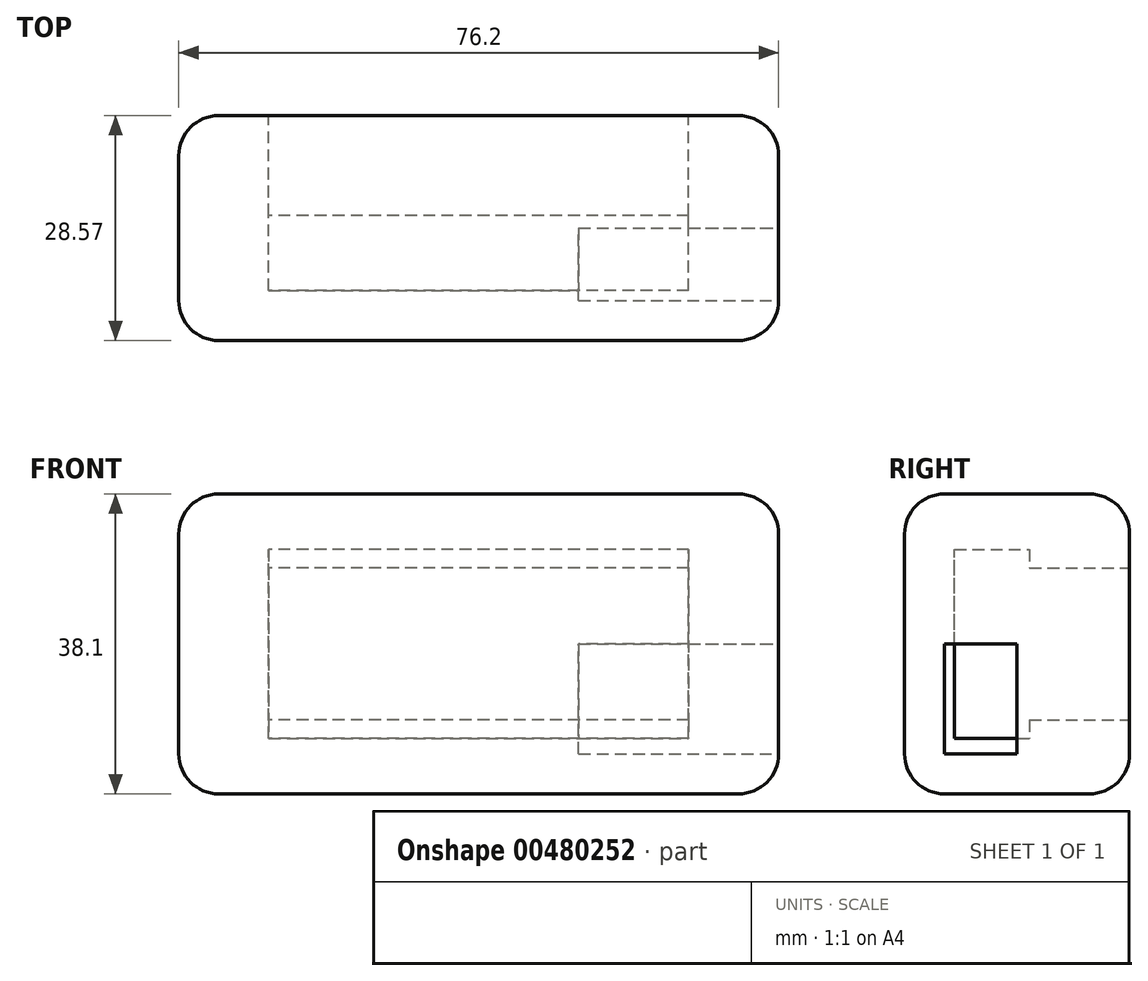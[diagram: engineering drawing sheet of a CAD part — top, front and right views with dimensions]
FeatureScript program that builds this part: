
annotation { "Feature Type Name" : "Feature", "Feature Type Description" : "" }
export const myFeature = defineFeature(function(context is Context, id is Id, definition is map)
    precondition{}
    {
        {
            var Q0;
            Q0=qCreatedBy(makeId("Front.planeOp"),FACE);
            var sketch = newSketch(context, id + "F0", { "sketchPlane" : qUnion([Q0])});
            skLineSegment(sketch, "E0.bottom", {"start": v(26.67, 9.65) * mm, "end": v(-26.67, 9.65) * mm});
            skLineSegment(sketch, "E0.top", {"start": v(26.67, -9.65) * mm, "end": v(-26.67, -9.65) * mm});
            skLineSegment(sketch, "E0.left", {"start": v(26.67, 9.65) * mm, "end": v(26.67, -9.65) * mm});
            skLineSegment(sketch, "E0.right", {"start": v(-26.67, 9.65) * mm, "end": v(-26.67, -9.65) * mm});
            skPoint(sketch, "E0.middle", {"position": v(0, 0) * mm});
            skLineSegment(sketch, "E1.bottom", {"start": v(38.1, 19.05) * mm, "end": v(-38.1, 19.05) * mm});
            skLineSegment(sketch, "E1.top", {"start": v(38.1, -19.05) * mm, "end": v(-38.1, -19.05) * mm});
            skLineSegment(sketch, "E1.left", {"start": v(38.1, 19.05) * mm, "end": v(38.1, -19.05) * mm});
            skLineSegment(sketch, "E1.right", {"start": v(-38.1, 19.05) * mm, "end": v(-38.1, -19.05) * mm});
            skSolve(sketch);
        }
        {
            var Q0;
            Q0=makeQuery(id+"F0.imprint","IMPRINT",FACE,{"disambiguationData":[TD([[makeQuery(id+"F0.imprint","IMPRINT",EDGE,{"derivedFrom":sQuery(id+"F0.wireOp",EDGE,"E0.bottom")}),-1.0]])]});
            extrude(context, id + "F1", {"entities" : qUnion([Q0]), "depth" : 12.7 * mm});
        }
        {
            var Q0;
            Q0=makeQuery(id+"F1.opExtrude","CAP_FACE",FACE,{"disambiguationData":[OSD([sQuery(id+"F0.wireOp",EDGE,"E0.bottom"),sQuery(id+"F0.wireOp",EDGE,"E0.top"),sQuery(id+"F0.wireOp",EDGE,"E0.left"),sQuery(id+"F0.wireOp",EDGE,"E0.right"),sQuery(id+"F0.wireOp",EDGE,"E1.bottom"),sQuery(id+"F0.wireOp",EDGE,"E1.top"),sQuery(id+"F0.wireOp",EDGE,"E1.left"),sQuery(id+"F0.wireOp",EDGE,"E1.right")])],"isStart":false});
            var sketch = newSketch(context, id + "F2", { "sketchPlane" : qUnion([Q0])});
            skLineSegment(sketch, "E2.bottom", {"start": v(26.67, 12) * mm, "end": v(-26.67, 12) * mm});
            skLineSegment(sketch, "E2.top", {"start": v(26.67, -12) * mm, "end": v(-26.67, -12) * mm});
            skLineSegment(sketch, "E2.left", {"start": v(26.67, 12) * mm, "end": v(26.67, -12) * mm});
            skLineSegment(sketch, "E2.right", {"start": v(-26.67, 12) * mm, "end": v(-26.67, -12) * mm});
            skPoint(sketch, "E2.middle", {"position": v(0, 0) * mm});
            skSolve(sketch);
        }
        {
            var Q0;
            {var subQ6=sQuery(id+"F2.wireOp",EDGE,"E2.bottom");Q0=makeQuery(id+"F2.imprint","IMPRINT",FACE,{"disambiguationData":[TD([[makeQuery(id+"F2.imprint","IMPRINT",EDGE,{"derivedFrom":subQ6}),-1.0]])]});}
            extrude(context, id + "F3", {"entities" : qUnion([Q0]), "operationType" : NewBodyOperationType.ADD, "depth" : 12.7 * mm});
        }
        {
            var Q0;
            Q0=makeQuery(id+"F3.opExtrude","SWEPT_FACE",FACE,{"disambiguationData":[OSD([sQuery(id+"F2.wireOp",EDGE,"E2.bottom")])]});
            var sketch = newSketch(context, id + "F4", { "sketchPlane" : qUnion([Q0])});
            skLineSegment(sketch, "E3.bottom", {"start": v(38.1, 28.58) * mm, "end": v(-38.1, 28.58) * mm});
            skLineSegment(sketch, "E3.top", {"start": v(38.1, 22.23) * mm, "end": v(-38.1, 22.23) * mm});
            skLineSegment(sketch, "E3.left", {"start": v(38.1, 28.57) * mm, "end": v(38.1, 22.23) * mm});
            skLineSegment(sketch, "E3.right", {"start": v(-38.1, 28.57) * mm, "end": v(-38.1, 22.23) * mm});
            skPoint(sketch, "E3.middle", {"position": v(0, 25.4) * mm});
            skSolve(sketch);
        }
        {
            var Q0;
            Q0=makeQuery(id+"F4.imprint","IMPRINT",FACE,{"disambiguationData":[TD([[makeQuery(id+"F4.imprint","IMPRINT",EDGE,{"derivedFrom":sQuery(id+"F4.wireOp",EDGE,"E3.bottom")}),1.0]])]});
            var Q1;
            {var subQ1=sQuery(id+"F2.wireOp",EDGE,"E2.bottom");var subQ6=makeQuery(id+"F3.opExtrude","CAP_EDGE",EDGE,{"disambiguationData":[OSD([subQ1])],"isStart":false});Q1=makeQuery(id+"F4.imprint","IMPRINT",FACE,{"disambiguationData":[TD([[makeQuery(id+"F4.imprint","IMPRINT",EDGE,{"derivedFrom":subQ6}),1.0]])]});}
            var Q2;
            {var subQ0=sQuery(id+"F0.wireOp",EDGE,"E1.top");Q2=makeQuery(id+"F3.boolean.opBoolean","MERGE",FACE,{"derivedFrom":[makeQuery(id+"F1.opExtrude","SWEPT_FACE",FACE,{"disambiguationData":[OSD([subQ0])]}),makeQuery(id+"F3.opExtrude","SWEPT_FACE",FACE,{"disambiguationData":[OSD([subQ0])]})]});}
            extrude(context, id + "F5", {"entities" : qUnion([Q0, Q1]), "operationType" : NewBodyOperationType.ADD, "endBound" : BoundingType.UP_TO_SURFACE, "endBoundEntityFace" : qUnion([Q2]), "depth" : 25.4 * mm});
        }
        {
            var Q0;
            Q0=makeQuery(id+"F5.opExtrude","CAP_FACE",FACE,{"disambiguationData":[OSD([sQuery(id+"F4.wireOp",EDGE,"E3.bottom"),sQuery(id+"F4.wireOp",EDGE,"E3.top"),sQuery(id+"F4.wireOp",EDGE,"E3.left"),sQuery(id+"F4.wireOp",EDGE,"E3.right")])],"isStart":true});
            var Q1;
            {var subQ0=sQuery(id+"F0.wireOp",EDGE,"E1.bottom");Q1=makeQuery(id+"F3.boolean.opBoolean","MERGE",FACE,{"derivedFrom":[makeQuery(id+"F1.opExtrude","SWEPT_FACE",FACE,{"disambiguationData":[OSD([subQ0])]}),makeQuery(id+"F3.opExtrude","SWEPT_FACE",FACE,{"disambiguationData":[OSD([subQ0])]})]});}
            extrude(context, id + "F6", {"entities" : qUnion([Q0]), "operationType" : NewBodyOperationType.ADD, "endBound" : BoundingType.UP_TO_SURFACE, "endBoundEntityFace" : qUnion([Q1]), "depth" : 25.4 * mm});
        }
        {
            var Q0;
            Q0=makeQuery(id+"F1.opExtrude","CAP_EDGE",EDGE,{"disambiguationData":[OSD([sQuery(id+"F0.wireOp",EDGE,"E1.bottom")])],"isStart":true});
            var Q1;
            {var subQ0=sQuery(id+"F0.wireOp",EDGE,"E1.left");var subQ1=sQuery(id+"F0.wireOp",EDGE,"E1.bottom");Q1=makeQuery(id+"F6.boolean.opBoolean","MERGE",EDGE,{"derivedFrom":[makeQuery(id+"F3.boolean.opBoolean","MERGE",EDGE,{"derivedFrom":[makeQuery(id+"F1.opExtrude","SWEPT_EDGE",EDGE,{"disambiguationData":[OSD([subQ1,subQ0])]}),makeQuery(id+"F3.opExtrude","SWEPT_EDGE",EDGE,{"disambiguationData":[OSD([subQ1,subQ0])]})]}),makeQuery(id+"F6.opExtrude","CAP_EDGE",EDGE,{"disambiguationData":[OSD([sQuery(id+"F4.wireOp",EDGE,"E3.left")])],"isStart":false})]});}
            var Q2;
            Q2=makeQuery(id+"F6.opExtrude","CAP_EDGE",EDGE,{"disambiguationData":[OSD([sQuery(id+"F4.wireOp",EDGE,"E3.bottom")])],"isStart":false});
            var Q3;
            {var subQ0=sQuery(id+"F0.wireOp",EDGE,"E1.right");var subQ1=sQuery(id+"F0.wireOp",EDGE,"E1.bottom");Q3=makeQuery(id+"F6.boolean.opBoolean","MERGE",EDGE,{"derivedFrom":[makeQuery(id+"F3.boolean.opBoolean","MERGE",EDGE,{"derivedFrom":[makeQuery(id+"F1.opExtrude","SWEPT_EDGE",EDGE,{"disambiguationData":[OSD([subQ1,subQ0])]}),makeQuery(id+"F3.opExtrude","SWEPT_EDGE",EDGE,{"disambiguationData":[OSD([subQ1,subQ0])]})]}),makeQuery(id+"F6.opExtrude","CAP_EDGE",EDGE,{"disambiguationData":[OSD([sQuery(id+"F4.wireOp",EDGE,"E3.right")])],"isStart":false})]});}
            var Q4;
            Q4=makeQuery(id+"F1.opExtrude","CAP_EDGE",EDGE,{"disambiguationData":[OSD([sQuery(id+"F0.wireOp",EDGE,"E1.right")])],"isStart":true});
            var Q5;
            Q5=makeQuery(id+"F1.opExtrude","CAP_EDGE",EDGE,{"disambiguationData":[OSD([sQuery(id+"F0.wireOp",EDGE,"E1.left")])],"isStart":true});
            var Q6;
            Q6=makeQuery(id+"F1.opExtrude","CAP_EDGE",EDGE,{"disambiguationData":[OSD([sQuery(id+"F0.wireOp",EDGE,"E1.top")])],"isStart":true});
            var Q7;
            {var subQ0=sQuery(id+"F0.wireOp",EDGE,"E1.left");var subQ1=sQuery(id+"F0.wireOp",EDGE,"E1.top");Q7=makeQuery(id+"F5.boolean.opBoolean","MERGE",EDGE,{"derivedFrom":[makeQuery(id+"F3.boolean.opBoolean","MERGE",EDGE,{"derivedFrom":[makeQuery(id+"F1.opExtrude","SWEPT_EDGE",EDGE,{"disambiguationData":[OSD([subQ1,subQ0])]}),makeQuery(id+"F3.opExtrude","SWEPT_EDGE",EDGE,{"disambiguationData":[OSD([subQ1,subQ0])]})]}),makeQuery(id+"F5.opExtrude","CAP_EDGE",EDGE,{"disambiguationData":[OSD([sQuery(id+"F4.wireOp",EDGE,"E3.left")])],"isStart":false})]});}
            var Q8;
            {var subQ0=sQuery(id+"F0.wireOp",EDGE,"E1.right");var subQ1=sQuery(id+"F0.wireOp",EDGE,"E1.top");Q8=makeQuery(id+"F5.boolean.opBoolean","MERGE",EDGE,{"derivedFrom":[makeQuery(id+"F3.boolean.opBoolean","MERGE",EDGE,{"derivedFrom":[makeQuery(id+"F1.opExtrude","SWEPT_EDGE",EDGE,{"disambiguationData":[OSD([subQ1,subQ0])]}),makeQuery(id+"F3.opExtrude","SWEPT_EDGE",EDGE,{"disambiguationData":[OSD([subQ1,subQ0])]})]}),makeQuery(id+"F5.opExtrude","CAP_EDGE",EDGE,{"disambiguationData":[OSD([sQuery(id+"F4.wireOp",EDGE,"E3.right")])],"isStart":false})]});}
            var Q9;
            Q9=makeQuery(id+"F5.opExtrude","CAP_EDGE",EDGE,{"disambiguationData":[OSD([sQuery(id+"F4.wireOp",EDGE,"E3.bottom")])],"isStart":false});
            var Q10;
            {var subQ0=sQuery(id+"F4.wireOp",EDGE,"E3.left");var subQ1=sQuery(id+"F4.wireOp",EDGE,"E3.bottom");Q10=makeQuery(id+"F6.boolean.opBoolean","MERGE",EDGE,{"derivedFrom":[makeQuery(id+"F5.opExtrude","SWEPT_EDGE",EDGE,{"disambiguationData":[OSD([subQ1,subQ0])]}),makeQuery(id+"F6.opExtrude","SWEPT_EDGE",EDGE,{"disambiguationData":[OSD([subQ1,subQ0])]})]});}
            var Q11;
            {var subQ0=sQuery(id+"F4.wireOp",EDGE,"E3.right");var subQ1=sQuery(id+"F4.wireOp",EDGE,"E3.bottom");Q11=makeQuery(id+"F6.boolean.opBoolean","MERGE",EDGE,{"derivedFrom":[makeQuery(id+"F5.opExtrude","SWEPT_EDGE",EDGE,{"disambiguationData":[OSD([subQ1,subQ0])]}),makeQuery(id+"F6.opExtrude","SWEPT_EDGE",EDGE,{"disambiguationData":[OSD([subQ1,subQ0])]})]});}
            fillet(context, id + "F7", {"entities" : qUnion([Q0, Q1, Q2, Q3, Q4, Q5, Q6, Q7, Q8, Q9, Q10, Q11]), "radius" : 5.08 * mm, "tangentPropagation" : true, "allowEdgeOverflow" : false});
        }
        {
            var Q0;
            {var subQ0=sQuery(id+"F4.wireOp",EDGE,"E3.left");var subQ1=sQuery(id+"F0.wireOp",EDGE,"E1.left");Q0=makeQuery(id+"F6.boolean.opBoolean","MERGE",FACE,{"derivedFrom":[makeQuery(id+"F5.boolean.opBoolean","MERGE",FACE,{"derivedFrom":[makeQuery(id+"F3.boolean.opBoolean","MERGE",FACE,{"derivedFrom":[makeQuery(id+"F1.opExtrude","SWEPT_FACE",FACE,{"disambiguationData":[OSD([subQ1])]}),makeQuery(id+"F3.opExtrude","SWEPT_FACE",FACE,{"disambiguationData":[OSD([subQ1])]})]}),makeQuery(id+"F5.opExtrude","SWEPT_FACE",FACE,{"disambiguationData":[OSD([subQ0])]})]}),makeQuery(id+"F6.opExtrude","SWEPT_FACE",FACE,{"disambiguationData":[OSD([subQ0])]})]});}
            var sketch = newSketch(context, id + "F8", { "sketchPlane" : qUnion([Q0])});
            skLineSegment(sketch, "E4.bottom", {"start": v(-23.5, -13.97) * mm, "end": v(-14.29, -13.97) * mm});
            skLineSegment(sketch, "E4.top", {"start": v(-23.5, 0) * mm, "end": v(-14.29, 0) * mm});
            skLineSegment(sketch, "E4.left", {"start": v(-23.5, -13.97) * mm, "end": v(-23.5, 0) * mm});
            skLineSegment(sketch, "E4.right", {"start": v(-14.29, -13.97) * mm, "end": v(-14.29, 0) * mm});
            skSolve(sketch);
        }
        {
            var Q0;
            Q0=makeQuery(id+"F8.imprint","IMPRINT",FACE,{"disambiguationData":[TD([[makeQuery(id+"F8.imprint","IMPRINT",EDGE,{"derivedFrom":sQuery(id+"F8.wireOp",EDGE,"E4.bottom")}),1.0]])]});
            extrude(context, id + "F9", {"entities" : qUnion([Q0]), "operationType" : NewBodyOperationType.REMOVE, "oppositeDirection" : true, "depth" : 25.4 * mm});
        }
    });
